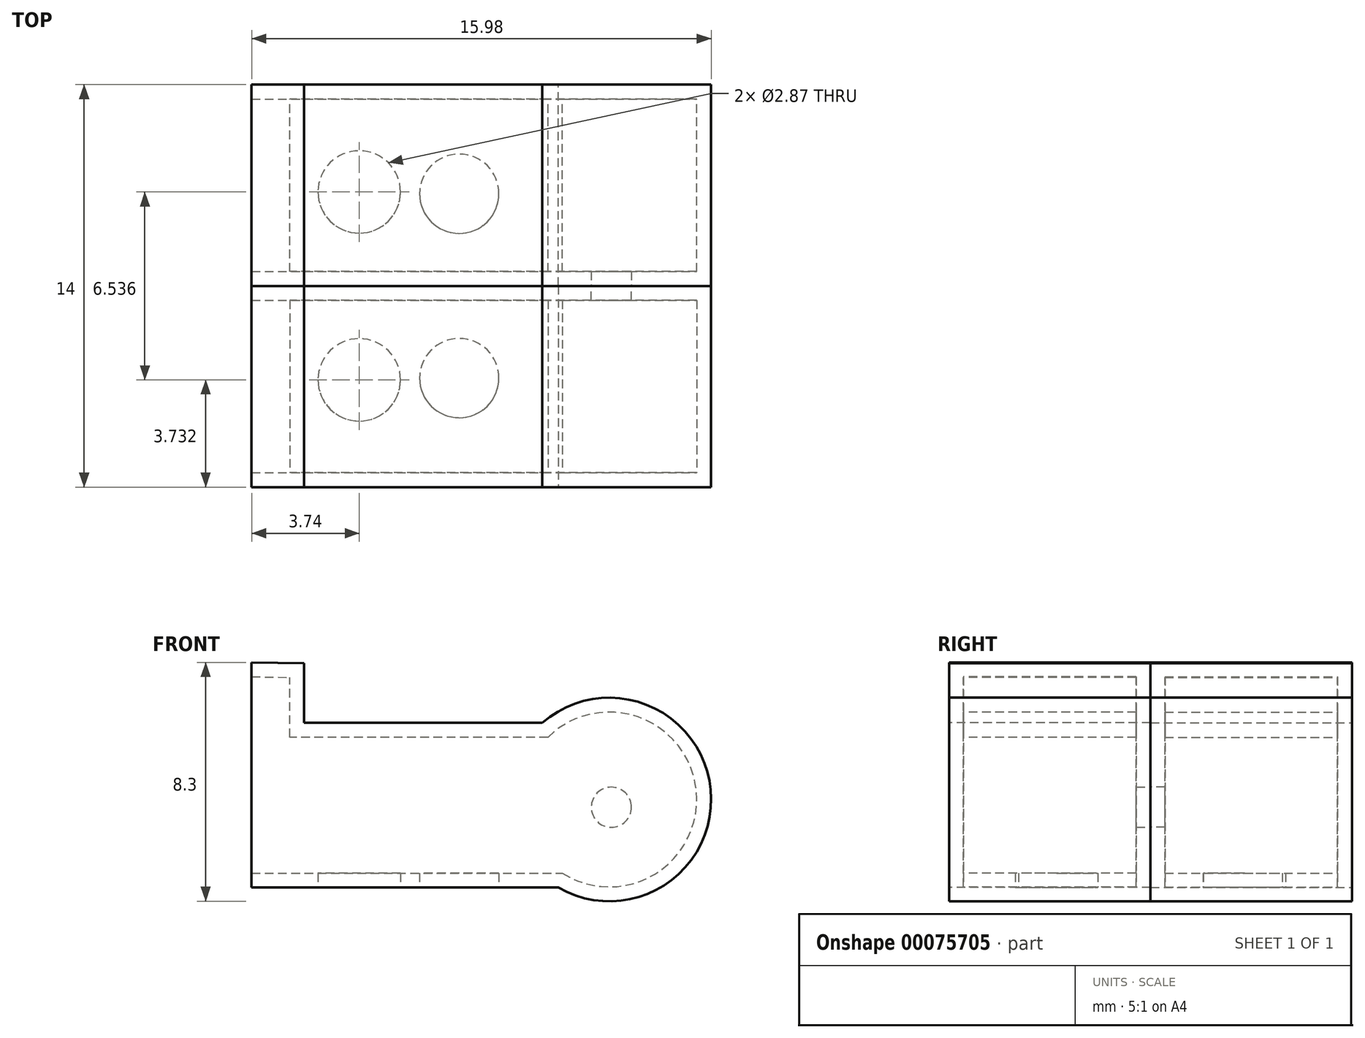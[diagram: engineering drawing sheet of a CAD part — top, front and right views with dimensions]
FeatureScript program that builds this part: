
annotation { "Feature Type Name" : "Feature", "Feature Type Description" : "" }
export const myFeature = defineFeature(function(context is Context, id is Id, definition is map)
    precondition{}
    {
        {
            var Q0;
            Q0=qCreatedBy(makeId("Front.planeOp"),FACE);
            var sketch = newSketch(context, id + "F0", { "sketchPlane" : qUnion([Q0])});
            skLineSegment(sketch, "E0", {"start": v(-3.74, -14.53) * mm, "end": v(7.32, -14.53) * mm});
            skLineSegment(sketch, "E1", {"start": v(7.32, -14.53) * mm, "end": v(7.32, -8.8) * mm});
            skLineSegment(sketch, "E2", {"start": v(7.32, -8.8) * mm, "end": v(-1.91, -8.8) * mm});
            skLineSegment(sketch, "E3", {"start": v(-1.91, -8.8) * mm, "end": v(-1.91, -6.73) * mm});
            skLineSegment(sketch, "E4", {"start": v(-3.74, -6.7) * mm, "end": v(-1.91, -6.73) * mm});
            skLineSegment(sketch, "E5", {"start": v(-3.74, -6.7) * mm, "end": v(-3.74, -14.53) * mm});
            skCircle(sketch, "E6", {"center": v(8.7, -11.46) * mm, "radius": 3.54 * mm});
            skSolve(sketch);
        }
        {
            var Q0;
            {var subQ0=sQuery(id+"F0.wireOp",EDGE,"E1");Q0=makeQuery(id+"F0.imprint","IMPRINT",FACE,{"disambiguationData":[TD([[makeQuery(id+"F0.imprint","IMPRINT",EDGE,{"derivedFrom":subQ0}),-1.0]])]});}
            var Q1;
            {var subQ0=sQuery(id+"F0.wireOp",EDGE,"E1");Q1=makeQuery(id+"F0.imprint","IMPRINT",FACE,{"disambiguationData":[TD([[makeQuery(id+"F0.imprint","IMPRINT",EDGE,{"derivedFrom":subQ0}),1.0]])]});}
            var Q2;
            {var subQ0=sQuery(id+"F0.wireOp",EDGE,"E3");Q2=makeQuery(id+"F0.imprint","IMPRINT",FACE,{"disambiguationData":[TD([[makeQuery(id+"F0.imprint","IMPRINT",EDGE,{"derivedFrom":subQ0}),1.0]])]});}
            extrude(context, id + "F1", {"entities" : qUnion([Q0, Q1, Q2]), "depth" : 7 * mm});
        }
        {
            var Q0;
            Q0=makeQuery(id+"F1.opExtrude","SWEPT_FACE",FACE,{"disambiguationData":[OSD([sQuery(id+"F0.wireOp",EDGE,"E5")])]});
            shell(context, id + "F2", {"entities" : qUnion([Q0]), "thickness" : .5 * mm});
        }
        {
            var Q0;
            Q0=makeQuery(id+"F1.opExtrude","SWEPT_FACE",FACE,{"disambiguationData":[OSD([sQuery(id+"F0.wireOp",EDGE,"E0")])]});
            var sketch = newSketch(context, id + "F3", { "sketchPlane" : qUnion([Q0])});
            skCircle(sketch, "E7", {"center": v(0, 3.73) * mm, "radius": 1.43 * mm});
            skCircle(sketch, "E8", {"center": v(3.48, 3.8) * mm, "radius": 1.38 * mm});
            skSolve(sketch);
        }
        {
            var Q0;
            Q0=makeQuery(id+"F3.imprint","IMPRINT",FACE,{"disambiguationData":[TD([[makeQuery(id+"F3.imprint","IMPRINT",EDGE,{"derivedFrom":sQuery(id+"F3.wireOp",EDGE,"E8")}),1.0]])]});
            var Q1;
            Q1=makeQuery(id+"F3.imprint","IMPRINT",FACE,{"disambiguationData":[TD([[makeQuery(id+"F3.imprint","IMPRINT",EDGE,{"derivedFrom":sQuery(id+"F3.wireOp",EDGE,"E7")}),1.0]])]});
            extrude(context, id + "F4", {"entities" : qUnion([Q0, Q1]), "operationType" : NewBodyOperationType.REMOVE, "endBound" : BoundingType.UP_TO_NEXT, "oppositeDirection" : true, "depth" : 25 * mm});
        }
        {
            var Q0;
            Q0=makeQuery(id+"F1.opExtrude","CAP_FACE",FACE,{"disambiguationData":[OSD([sQuery(id+"F0.wireOp",EDGE,"E0"),sQuery(id+"F0.wireOp",EDGE,"E2"),sQuery(id+"F0.wireOp",EDGE,"E3"),sQuery(id+"F0.wireOp",EDGE,"E4"),sQuery(id+"F0.wireOp",EDGE,"E5"),sQuery(id+"F0.wireOp",EDGE,"E6")])],"isStart":false});
            var sketch = newSketch(context, id + "F5", { "sketchPlane" : qUnion([Q0])});
            skSolve(sketch);
        }
        {
            var Q0;
            Q0=makeQuery(id+"F5.imprint","IMPRINT",FACE,{"disambiguationData":[TD([[makeQuery(id+"F5.imprint","IMPRINT",EDGE,{"derivedFrom":makeQuery(id+"F1.opExtrude","CAP_EDGE",EDGE,{"disambiguationData":[OSD([sQuery(id+"F0.wireOp",EDGE,"E0")])],"isStart":false})}),1.0]])]});
            var sketch = newSketch(context, id + "F6", { "sketchPlane" : qUnion([Q0])});
            skCircle(sketch, "E9", {"center": v(8.76, -11.73) * mm, "radius": 0.7 * mm});
            skSolve(sketch);
        }
        {
            var Q0;
            Q0=makeQuery(id+"F6.imprint","IMPRINT",FACE,{"disambiguationData":[TD([[makeQuery(id+"F6.imprint","IMPRINT",EDGE,{"derivedFrom":sQuery(id+"F6.wireOp",EDGE,"E9")}),1.0]])]});
            extrude(context, id + "F7", {"entities" : qUnion([Q0]), "operationType" : NewBodyOperationType.REMOVE, "endBound" : BoundingType.UP_TO_NEXT, "oppositeDirection" : true, "depth" : 3.7 * mm});
        }
        {
            var Q0;
            Q0=makeQuery(id+"F1.opExtrude","SWEPT_BODY",BODY,{"disambiguationData":[OSD([sQuery(id+"F0.wireOp",EDGE,"E0"),sQuery(id+"F0.wireOp",EDGE,"E2"),sQuery(id+"F0.wireOp",EDGE,"E3"),sQuery(id+"F0.wireOp",EDGE,"E4"),sQuery(id+"F0.wireOp",EDGE,"E5"),sQuery(id+"F0.wireOp",EDGE,"E6")])]});
            var Q1;
            Q1=makeQuery(id+"F5.imprint","IMPRINT",FACE,{"disambiguationData":[TD([[makeQuery(id+"F5.imprint","IMPRINT",EDGE,{"derivedFrom":makeQuery(id+"F1.opExtrude","CAP_EDGE",EDGE,{"disambiguationData":[OSD([sQuery(id+"F0.wireOp",EDGE,"E0")])],"isStart":false})}),1.0]])]});
            mirror(context, id + "F8", {"entities" : qUnion([Q0]), "mirrorPlane" : qUnion([Q1])});
        }
    });
